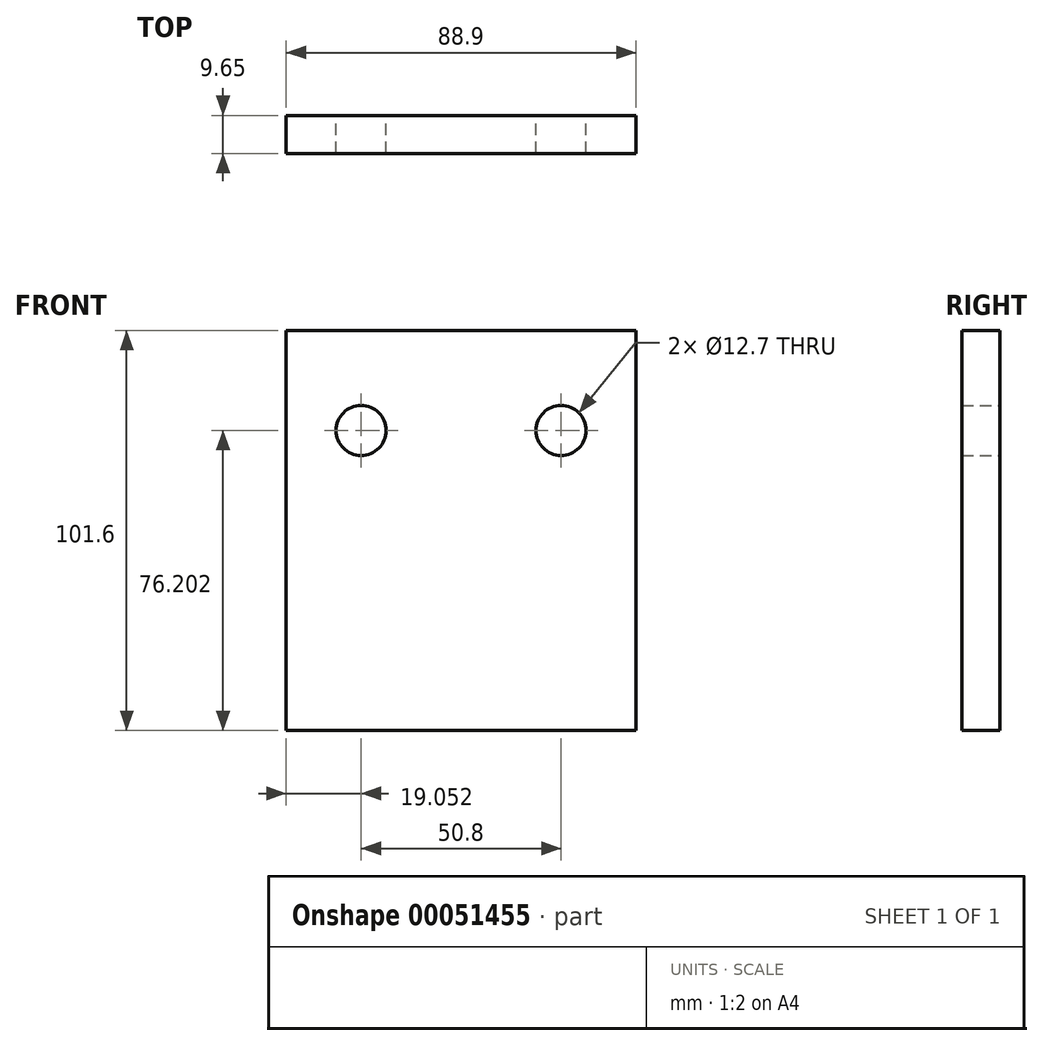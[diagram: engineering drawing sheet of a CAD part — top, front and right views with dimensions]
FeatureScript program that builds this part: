
annotation { "Feature Type Name" : "Feature", "Feature Type Description" : "" }
export const myFeature = defineFeature(function(context is Context, id is Id, definition is map)
    precondition{}
    {
        {
            var Q0;
            Q0=qCreatedBy(makeId("Front.planeOp"),FACE);
            var sketch = newSketch(context, id + "F0", { "sketchPlane" : qUnion([Q0])});
            skLineSegment(sketch, "E0.bottom", {"start": v(-48.5, 51.98) * mm, "end": v(40.4, 51.98) * mm});
            skLineSegment(sketch, "E0.top", {"start": v(-48.5, -49.62) * mm, "end": v(40.4, -49.62) * mm});
            skLineSegment(sketch, "E0.left", {"start": v(-48.5, 51.98) * mm, "end": v(-48.5, -49.62) * mm});
            skLineSegment(sketch, "E0.right", {"start": v(40.4, 51.98) * mm, "end": v(40.4, -49.62) * mm});
            skCircle(sketch, "E1", {"center": v(-29.45, 26.58) * mm, "radius": 6.35 * mm});
            skCircle(sketch, "E2", {"center": v(21.35, 26.58) * mm, "radius": 6.35 * mm});
            skLineSegment(sketch, "E3.0", {"start": v(21.35, 51.98) * mm, "end": v(21.35, -49.62) * mm, "construction": true});
            skLineSegment(sketch, "E4.0", {"start": v(-29.45, 51.98) * mm, "end": v(-29.45, -49.62) * mm, "construction": true});
            skLineSegment(sketch, "E5.0", {"start": v(-48.5, 26.58) * mm, "end": v(40.4, 26.58) * mm, "construction": true});
            skSolve(sketch);
        }
        {
            var Q0;
            Q0 = qSketchRegion(id + "F0", true);
            extrude(context, id + "F1", {"entities" : qUnion([Q0]), "depth" : 9.65 * mm});
        }
    });
